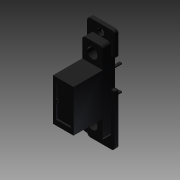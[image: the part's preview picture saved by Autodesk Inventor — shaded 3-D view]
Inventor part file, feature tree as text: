
AUTODESK INVENTOR PART (.ipt)
format: ipt  version: 2013 (Build 170138000, 138)  size: 182,272 bytes
history: native  units: in
note: dims shown in document units (in); Inventor stores cm internally (conversion verified against a paired STEP export)
features: sketch x8, extrude x6, reference x3, fillet x2, hole x2, plane x1, pattern_linear x1
ambient origin geometry x8: Origin, YZ Plane, XZ Plane, XY Plane, X Axis, Y Axis, Z Axis, Center Point
feature tree (23):
  plane  "Work Plane4"
  extrude  "Extrusion3"  Depth=0.25in
  extrude  "Extrusion4"  Depth=0.998in
  fillet  "Fillet2"  Radius=0.102in
  extrude  "Extrusion5"  Depth=1.26in
  fillet  "Fillet3"  Radius=0.335in
  hole  "Hole2"  [1 undecoded]
  hole  "Hole3"  [1 undecoded]
  extrude  "Extrusion6"  Depth=0.031in
  pattern_linear  "Rectangular Pattern1"  Spacing1=0.102in  [1 undecoded]
  extrude  "Extrusion7"  Depth=0.146in TaperAngle=0.0deg
  extrude  "Extrusion8"  Depth=0.7874in
  sketch  "Sketch4"  dims[d15=0.512in d16=0.25in]
  reference  "Reference4"
  sketch  "Sketch5"  dims[d17=0.356in d18=0.0in d19=0.998in d21=0.102in d22=0.0in]
  sketch  "Sketch6"  dims[d23=0.039in d24=1.26in d25=0.335in]
  sketch  "Sketch7"  dims[d26=0.047in d27=0.0in d28=0.039in]
  reference  "Reference5"
  reference  "Reference6"
  sketch  "Sketch8"  dims[d29=0.126in d30=0.75in d31=0.375in d32=0.25in d33=0.5635in d34=1.0in d35=0.8108in d36=1.087in]
  sketch  "Sketch9"  dims[d37=0.079in d38=0.75in d39=0.375in d40=0.25in d41=0.5635in d42=1.0in d43=0.8108in d44=0.031in]
  sketch  "Sketch10"  dims[d45=0.012in]
  sketch  "Sketch11"  dims[d46=0.474in d47=0.102in d48=0.146in d49=0.0in d50=0.7874in d52=0.3in d53=0.7874in d55=0.1in d56=0.276in d57=0.354in d58=0.043in d59=0.146in d60=0.0in d61=0.02in d62=0.0in]
note: 3 required parameter values undecoded (feature->parameter linkage not recoverable at this tier; creation-order binding heuristic only, values carry confidence <= 0.55)
